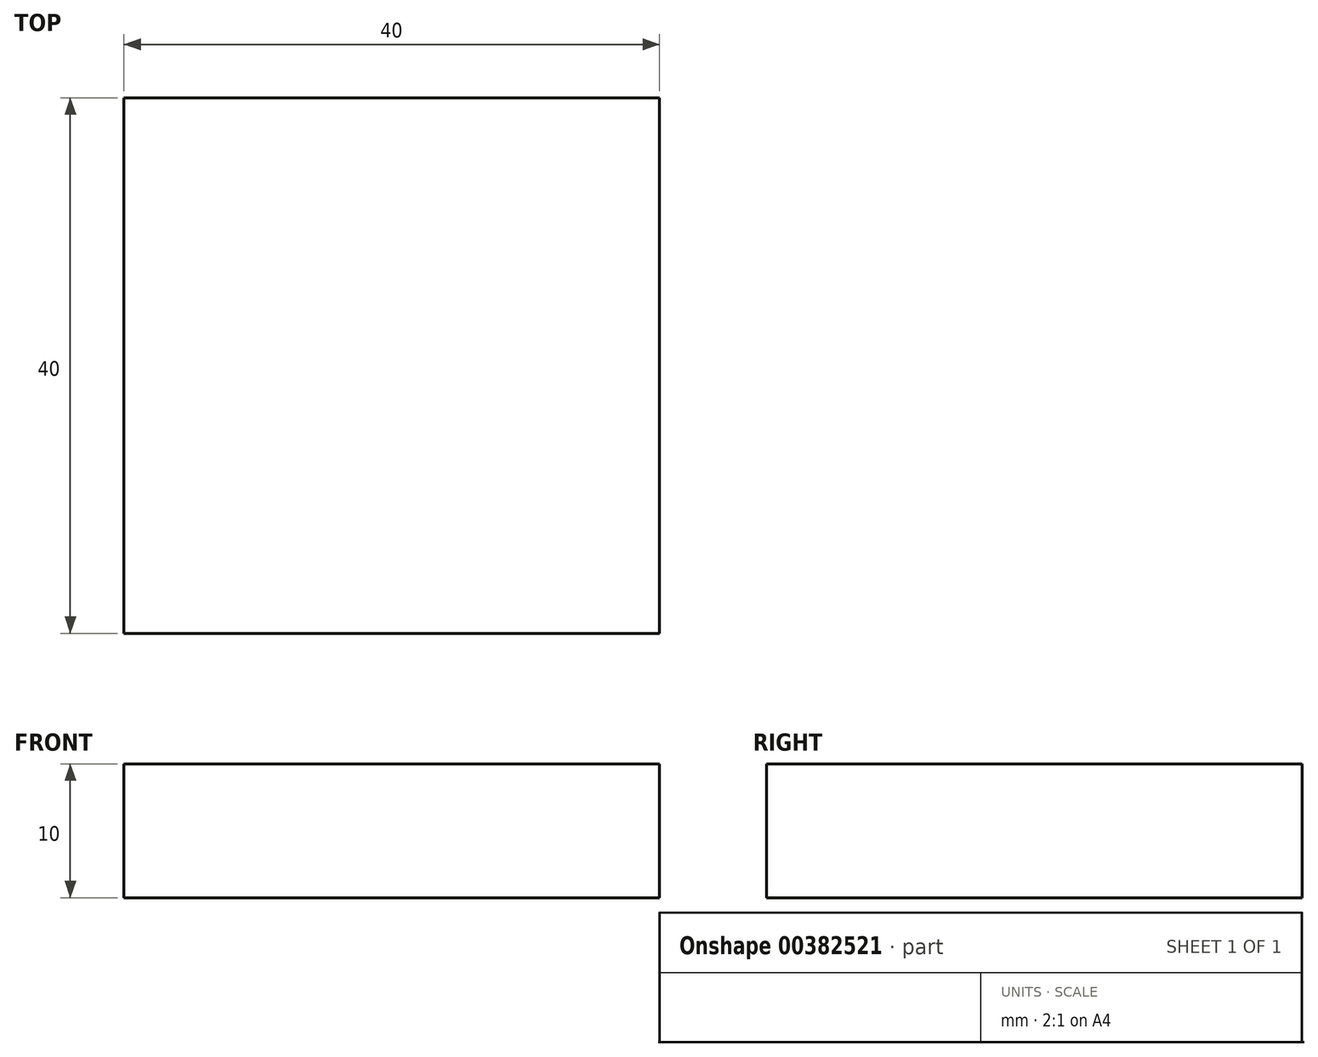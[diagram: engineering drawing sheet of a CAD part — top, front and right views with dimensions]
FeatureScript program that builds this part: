
annotation { "Feature Type Name" : "Feature", "Feature Type Description" : "" }
export const myFeature = defineFeature(function(context is Context, id is Id, definition is map)
    precondition{}
    {
        {
            var Q0;
            Q0=qCreatedBy(makeId("Top.planeOp"),FACE);
            var sketch = newSketch(context, id + "F0", { "sketchPlane" : qUnion([Q0])});
            skLineSegment(sketch, "E0.bottom", {"start": v(-28.54, 20) * mm, "end": v(-68.54, 20) * mm});
            skLineSegment(sketch, "E0.top", {"start": v(-28.54, -20) * mm, "end": v(-68.54, -20) * mm});
            skLineSegment(sketch, "E0.left", {"start": v(-28.54, 20) * mm, "end": v(-28.54, -20) * mm});
            skLineSegment(sketch, "E0.right", {"start": v(-68.54, 20) * mm, "end": v(-68.54, -20) * mm});
            skPoint(sketch, "E0.middle", {"position": v(-48.54, 0) * mm});
            skSolve(sketch);
        }
        {
            var Q0;
            Q0=makeQuery(id+"F0.imprint","IMPRINT",FACE,{"disambiguationData":[TD([[makeQuery(id+"F0.imprint","IMPRINT",EDGE,{"derivedFrom":sQuery(id+"F0.wireOp",EDGE,"E0.bottom")}),1.0]])]});
            extrude(context, id + "F1", {"entities" : qUnion([Q0]), "depth" : 10 * mm});
        }
    });
